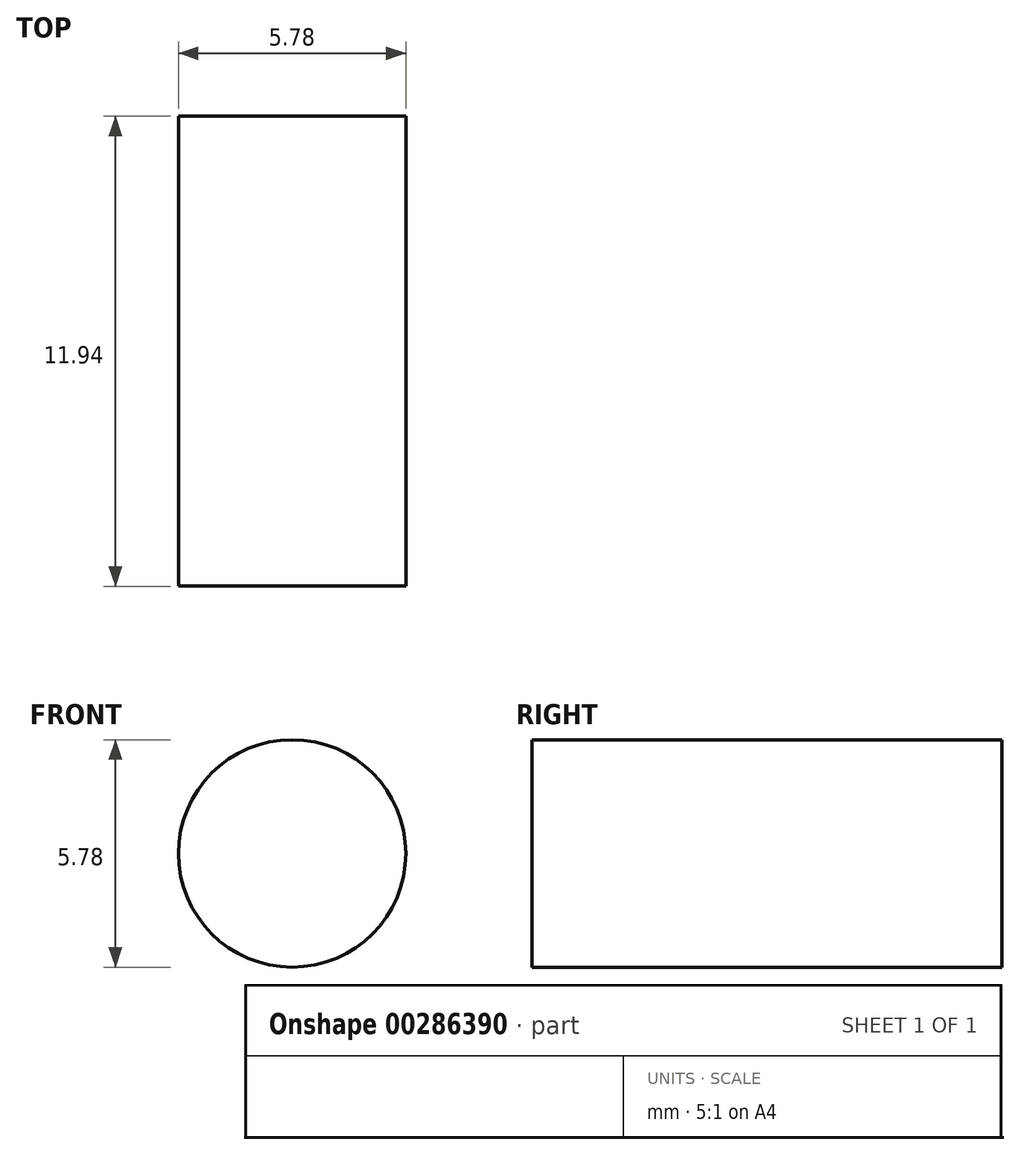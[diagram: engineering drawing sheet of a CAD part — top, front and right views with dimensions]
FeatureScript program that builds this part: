
annotation { "Feature Type Name" : "Feature", "Feature Type Description" : "" }
export const myFeature = defineFeature(function(context is Context, id is Id, definition is map)
    precondition{}
    {
        {
            var Q0;
            Q0=qCreatedBy(makeId("Front.planeOp"),FACE);
            var sketch = newSketch(context, id + "F0", { "sketchPlane" : qUnion([Q0])});
            skCircle(sketch, "E0", {"center": v(0, 0) * mm, "radius": 2.89 * mm});
            skSolve(sketch);
        }
        {
            var Q0;
            Q0 = qSketchRegion(id + "F0", true);
            extrude(context, id + "F1", {"entities" : qUnion([Q0]), "depth" : 11.94 * mm});
        }
    });
